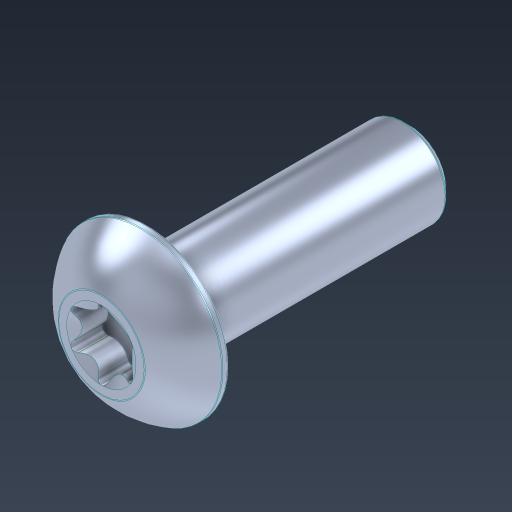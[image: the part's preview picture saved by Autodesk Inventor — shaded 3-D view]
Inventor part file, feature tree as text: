
AUTODESK INVENTOR PART (.ipt)
format: ipt  version: 2024.3 (Build 283343000, 343)  size: 218,112 bytes
history: native  units: in
note: dims shown in document units (in); Inventor stores cm internally (conversion verified against a paired STEP export)
features: fillet x1
ambient origin geometry x8: Origin, YZ Plane, XZ Plane, XY Plane, X Axis, Y Axis, Z Axis, Center Point
bodies: Solid1 (feature_tree)
feature tree (1):
  fillet  "Fillet1"  [1 undecoded]
note: 1 required parameter value undecoded (feature->parameter linkage not recoverable at this tier; creation-order binding heuristic only, values carry confidence <= 0.55)
